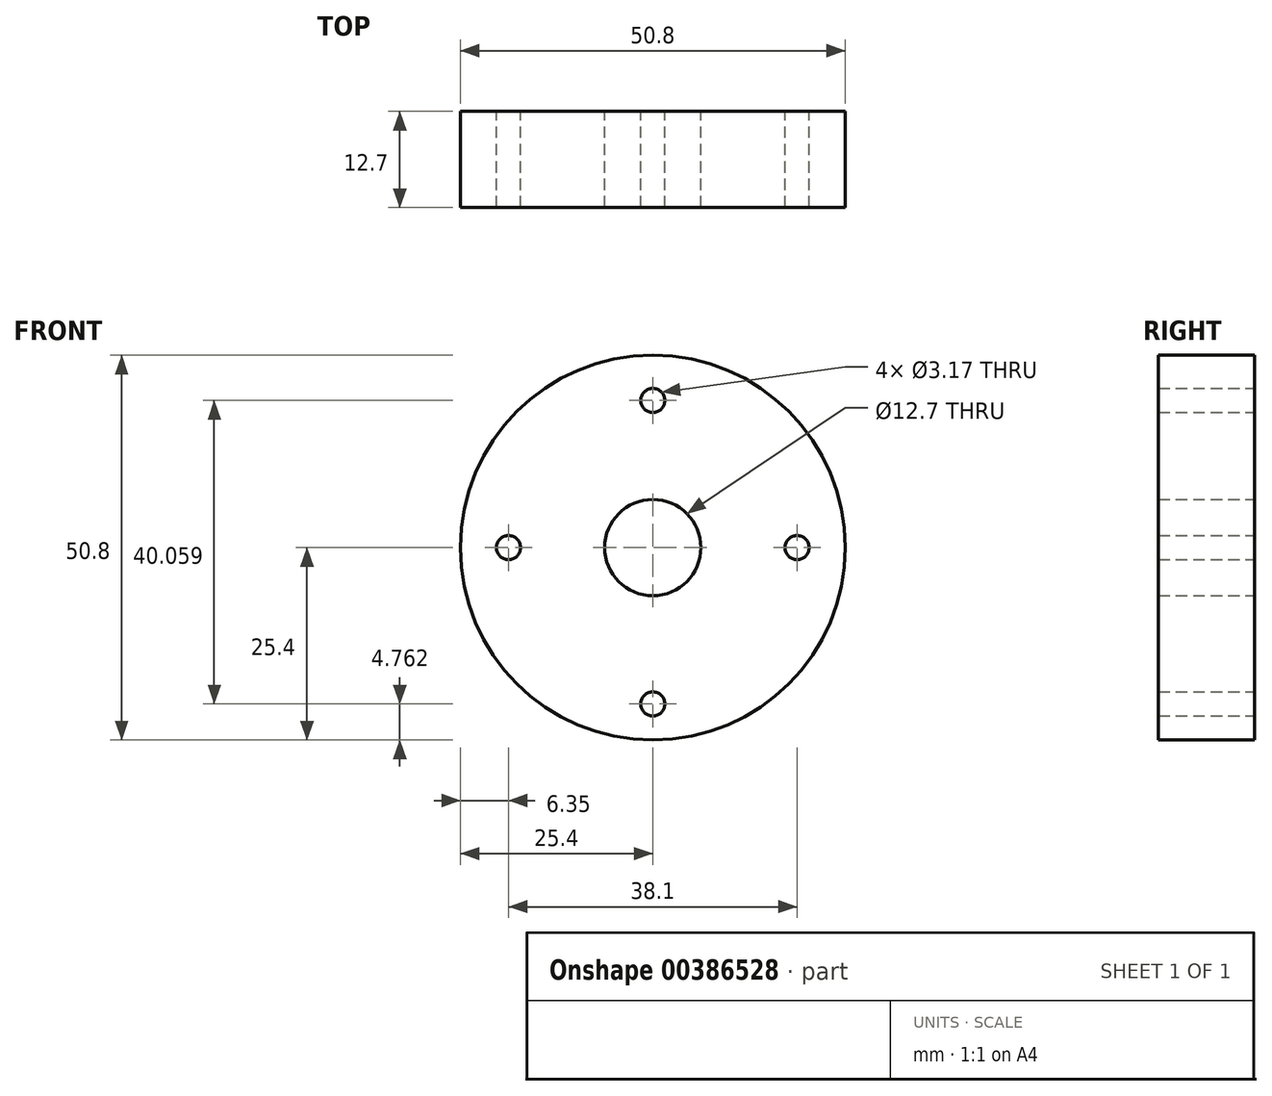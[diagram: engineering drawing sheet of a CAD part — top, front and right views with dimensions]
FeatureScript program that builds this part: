
annotation { "Feature Type Name" : "Feature", "Feature Type Description" : "" }
export const myFeature = defineFeature(function(context is Context, id is Id, definition is map)
    precondition{}
    {
        {
            var Q0;
            Q0=qCreatedBy(makeId("Front.planeOp"),FACE);
            var sketch = newSketch(context, id + "F0", { "sketchPlane" : qUnion([Q0])});
            skCircle(sketch, "E0", {"center": v(0, 0) * mm, "radius": 25.4 * mm});
            skCircle(sketch, "E1", {"center": v(0, 0) * mm, "radius": 22.23 * mm, "construction": true});
            skCircle(sketch, "E2", {"center": v(-19.05, 0) * mm, "radius": 1.59 * mm});
            skCircle(sketch, "E3", {"center": v(19.05, 0) * mm, "radius": 1.59 * mm});
            skCircle(sketch, "E4", {"center": v(0, -20.64) * mm, "radius": 1.59 * mm});
            skCircle(sketch, "E5", {"center": v(0, 19.42) * mm, "radius": 1.59 * mm});
            skCircle(sketch, "E6", {"center": v(0, 0) * mm, "radius": 6.35 * mm});
            skSolve(sketch);
        }
        {
            var Q0;
            Q0 = qSketchRegion(id + "F0", true);
            extrude(context, id + "F1", {"entities" : qUnion([Q0]), "depth" : 12.7 * mm});
        }
    });
